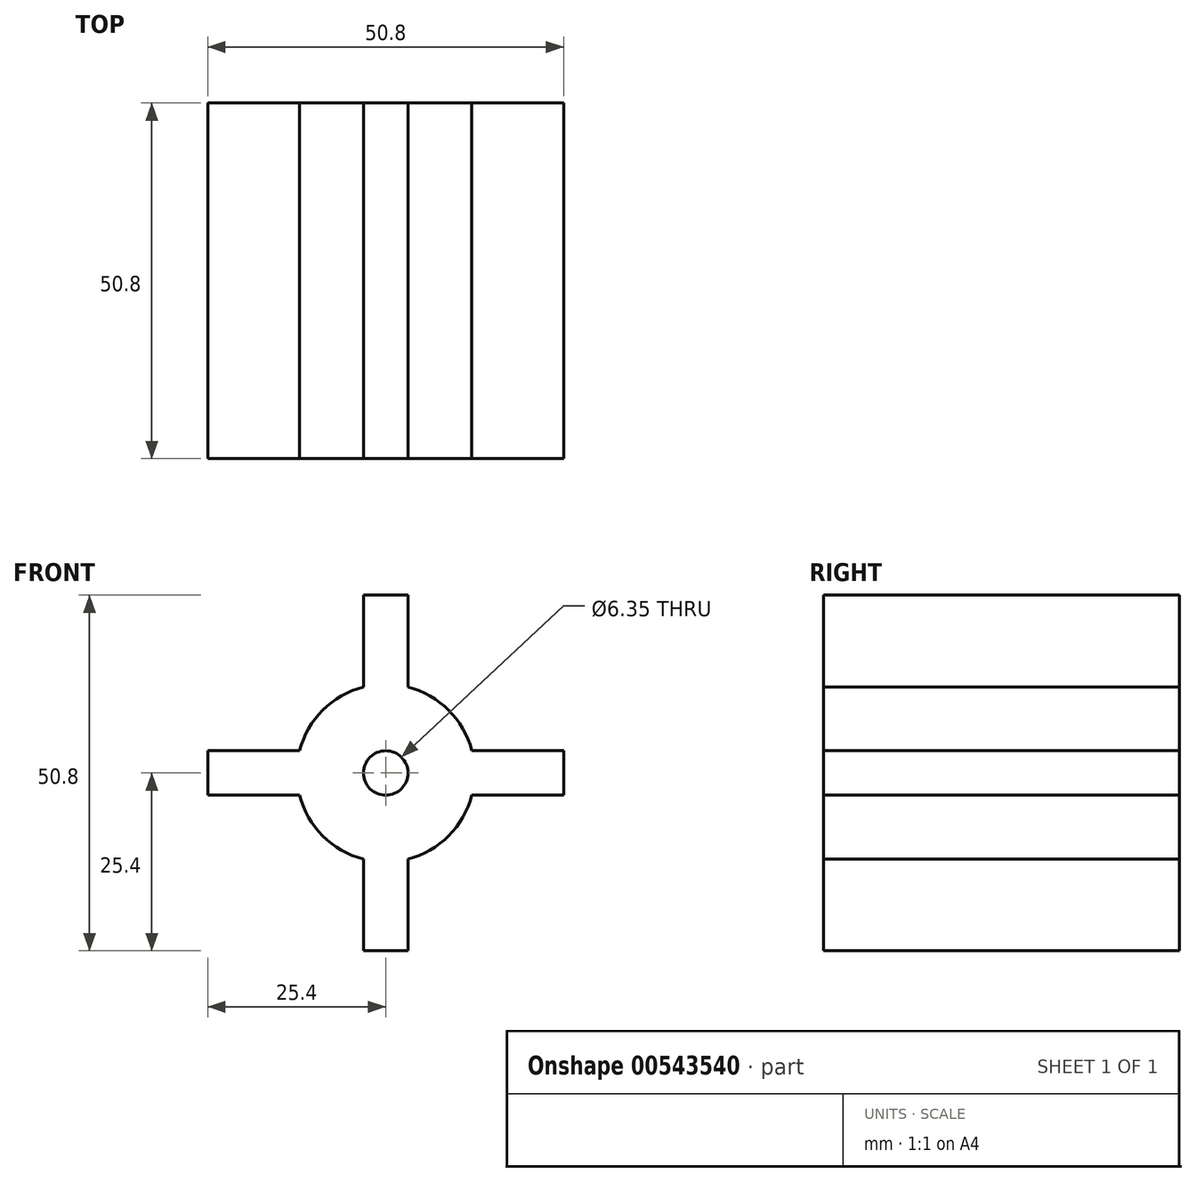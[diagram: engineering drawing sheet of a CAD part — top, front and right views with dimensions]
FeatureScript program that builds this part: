
annotation { "Feature Type Name" : "Feature", "Feature Type Description" : "" }
export const myFeature = defineFeature(function(context is Context, id is Id, definition is map)
    precondition{}
    {
        {
            var Q0;
            Q0=qCreatedBy(makeId("Front.planeOp"),FACE);
            var sketch = newSketch(context, id + "F0", { "sketchPlane" : qUnion([Q0])});
            skCircle(sketch, "E0", {"center": v(0, 0) * mm, "radius": 12.7 * mm});
            skSolve(sketch);
        }
        {
            var Q0;
            Q0=qSketchRegion(id+"F0",true);
            extrude(context, id + "F1", {"entities" : qUnion([Q0]), "depth" : 50.8 * mm, "offsetDistance" : 25.4 * mm});
        }
        {
            var Q0;
            Q0=qCreatedBy(makeId("Right.planeOp"),FACE);
            var sketch = newSketch(context, id + "F2", { "sketchPlane" : qUnion([Q0])});
            skLineSegment(sketch, "E1.bottom", {"start": v(-25.48, -0.06) * mm, "end": v(-25.4, 0) * mm});
            skLineSegment(sketch, "E2.bottom", {"start": v(0, 25.4) * mm, "end": v(-50.8, 25.4) * mm});
            skLineSegment(sketch, "E2.top", {"start": v(0, -25.4) * mm, "end": v(-50.8, -25.4) * mm});
            skLineSegment(sketch, "E2.left", {"start": v(0, 25.4) * mm, "end": v(0, -25.4) * mm});
            skLineSegment(sketch, "E2.right", {"start": v(-50.8, 25.4) * mm, "end": v(-50.8, -25.4) * mm});
            skPoint(sketch, "E2.middle", {"position": v(-25.4, 0) * mm});
            skLineSegment(sketch, "E3", {"start": v(-25.4, 0) * mm, "end": v(0, 0) * mm});
            skSolve(sketch);
        }
        {
            var Q0;
            Q0=qSketchRegion(id+"F2",true);
            extrude(context, id + "F3", {"entities" : qUnion([Q0]), "operationType" : NewBodyOperationType.ADD, "endBound" : BoundingType.SYMMETRIC, "depth" : 6.35 * mm, "offsetDistance" : 25.4 * mm});
        }
        {
            var Q0;
            Q0=qCreatedBy(makeId("Top.planeOp"),FACE);
            var sketch = newSketch(context, id + "F4", { "sketchPlane" : qUnion([Q0])});
            skLineSegment(sketch, "E4", {"start": v(0, 0) * mm, "end": v(0, -25.4) * mm});
            skLineSegment(sketch, "E5.bottom", {"start": v(-25.4, 0) * mm, "end": v(25.4, 0) * mm});
            skLineSegment(sketch, "E5.top", {"start": v(-25.4, -50.8) * mm, "end": v(25.4, -50.8) * mm});
            skLineSegment(sketch, "E5.left", {"start": v(-25.4, 0) * mm, "end": v(-25.4, -50.8) * mm});
            skLineSegment(sketch, "E5.right", {"start": v(25.4, 0) * mm, "end": v(25.4, -50.8) * mm});
            skPoint(sketch, "E5.middle", {"position": v(0, -25.4) * mm});
            skSolve(sketch);
        }
        {
            var Q0;
            Q0=makeQuery(id+"F4.imprint","IMPRINT",FACE,{"disambiguationData":[TD([[makeQuery(id+"F4.imprint","IMPRINT",EDGE,{"derivedFrom":sQuery(id+"F4.wireOp",EDGE,"E5.top")}),1.0]])]});
            extrude(context, id + "F5", {"entities" : qUnion([Q0]), "operationType" : NewBodyOperationType.ADD, "endBound" : BoundingType.SYMMETRIC, "depth" : 6.35 * mm, "offsetDistance" : 25.4 * mm});
        }
        {
            var Q0;
            Q0=makeQuery(id+"F5.boolean.opBoolean","MERGE",FACE,{"derivedFrom":[makeQuery(id+"F3.boolean.opBoolean","MERGE",FACE,{"derivedFrom":[makeQuery(id+"F1.opExtrude","CAP_FACE",FACE,{"disambiguationData":[OSD([sQuery(id+"F0.wireOp",EDGE,"E0")])],"isStart":true}),makeQuery(id+"F3.opExtrude","SWEPT_FACE",FACE,{"disambiguationData":[OSD([sQuery(id+"F2.wireOp",EDGE,"E2.left")])]})]}),makeQuery(id+"F5.opExtrude","SWEPT_FACE",FACE,{"disambiguationData":[OSD([sQuery(id+"F4.wireOp",EDGE,"E5.bottom")])]})]});
            var sketch = newSketch(context, id + "F6", { "sketchPlane" : qUnion([Q0])});
            skCircle(sketch, "E6", {"center": v(0, 0) * mm, "radius": 3.18 * mm});
            skSolve(sketch);
        }
        {
            var Q0;
            Q0=sQuery(id+"F6.wireOp",VERTEX,"E6.center");
            var Q1;
            Q1=makeQuery(id+"F1.opExtrude","SWEPT_BODY",BODY,{"disambiguationData":[OSD([sQuery(id+"F0.wireOp",EDGE,"E0")])]});
            hole(context, id + "F7", {"style" : HoleStyle.SIMPLE, "endStyle" : HoleEndStyle.THROUGH, "holeDiameter" : 6.35 * mm, "isTappedThrough" : true, "tappedDepth" : 12.7 * mm, "tapClearance" : 3, "startFromSketch" : true, "locations" : qUnion([Q0]), "scope" : qUnion([Q1])});
        }
    });
